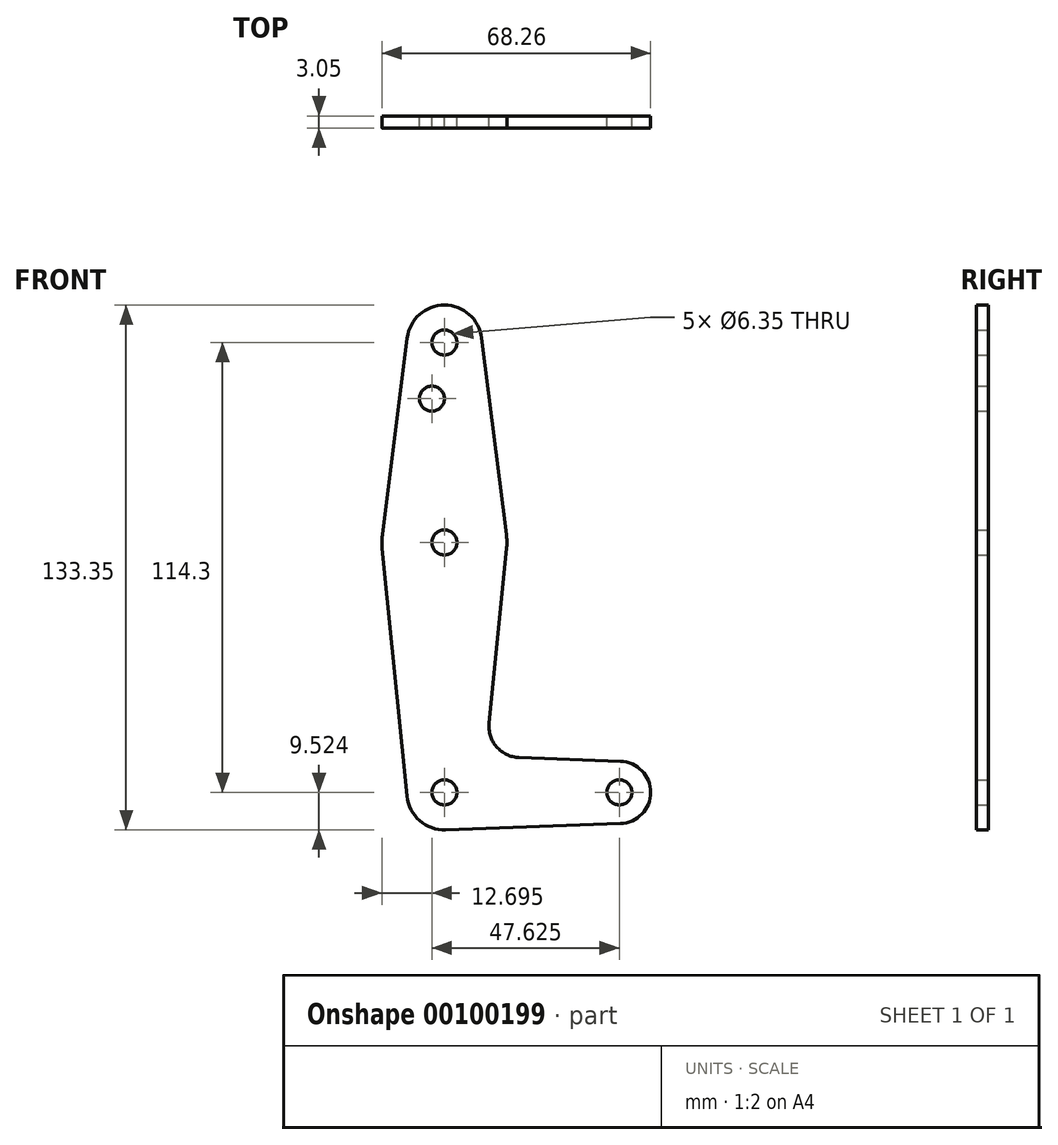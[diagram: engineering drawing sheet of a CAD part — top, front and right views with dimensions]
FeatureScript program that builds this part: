
annotation { "Feature Type Name" : "Feature", "Feature Type Description" : "" }
export const myFeature = defineFeature(function(context is Context, id is Id, definition is map)
    precondition{}
    {
        {
            var Q0;
            Q0=qCreatedBy(makeId("Front.planeOp"),FACE);
            var sketch = newSketch(context, id + "F0", { "sketchPlane" : qUnion([Q0])});
            skLineSegment(sketch, "E0", {"start": v(0, 61.57) * mm, "end": v(0, -52.73) * mm, "construction": true});
            skLineSegment(sketch, "E1", {"start": v(0, -52.73) * mm, "end": v(44.45, -52.73) * mm, "construction": true});
            skCircle(sketch, "E2", {"center": v(0, 61.57) * mm, "radius": 9.53 * mm});
            skCircle(sketch, "E3", {"center": v(0, 10.77) * mm, "radius": 15.88 * mm});
            skCircle(sketch, "E4", {"center": v(0, -52.73) * mm, "radius": 9.53 * mm});
            skCircle(sketch, "E5", {"center": v(44.45, -52.73) * mm, "radius": 7.94 * mm});
            skLineSegment(sketch, "E6", {"start": v(-9.45, 62.76) * mm, "end": v(-15.75, 12.76) * mm});
            skLineSegment(sketch, "E7", {"start": v(9.45, 62.76) * mm, "end": v(15.75, 12.76) * mm});
            skLineSegment(sketch, "E8", {"start": v(-15.8, 9.19) * mm, "end": v(-9.48, -53.68) * mm});
            skLineSegment(sketch, "E9", {"start": v(15.8, 9.19) * mm, "end": v(11.34, -35.13) * mm});
            skLineSegment(sketch, "E10", {"start": v(18.97, -43.87) * mm, "end": v(44.73, -44.8) * mm});
            skLineSegment(sketch, "E11", {"start": v(0.34, -62.25) * mm, "end": v(44.73, -60.66) * mm});
            skCircle(sketch, "E12", {"center": v(0, 61.57) * mm, "radius": 3.18 * mm});
            skCircle(sketch, "E13", {"center": v(0, 10.77) * mm, "radius": 3.18 * mm});
            skCircle(sketch, "E14", {"center": v(44.45, -52.73) * mm, "radius": 3.18 * mm});
            skCircle(sketch, "E15", {"center": v(-3.17, 47.3) * mm, "radius": 3.18 * mm});
            skArc(sketch, "E16.filletArc", {"start": v(11.34, -35.13) * mm, "mid": v(13.26, -41.15) * mm, "end": v(18.97, -43.87) * mm});
            skCircle(sketch, "E17", {"center": v(0, -52.73) * mm, "radius": 3.18 * mm});
            skSolve(sketch);
        }
        {
            var Q0;
            Q0 = qSketchRegion(id + "F0", true);
            extrude(context, id + "F1", {"entities" : qUnion([Q0]), "depth" : 3.05 * mm});
        }
    });
